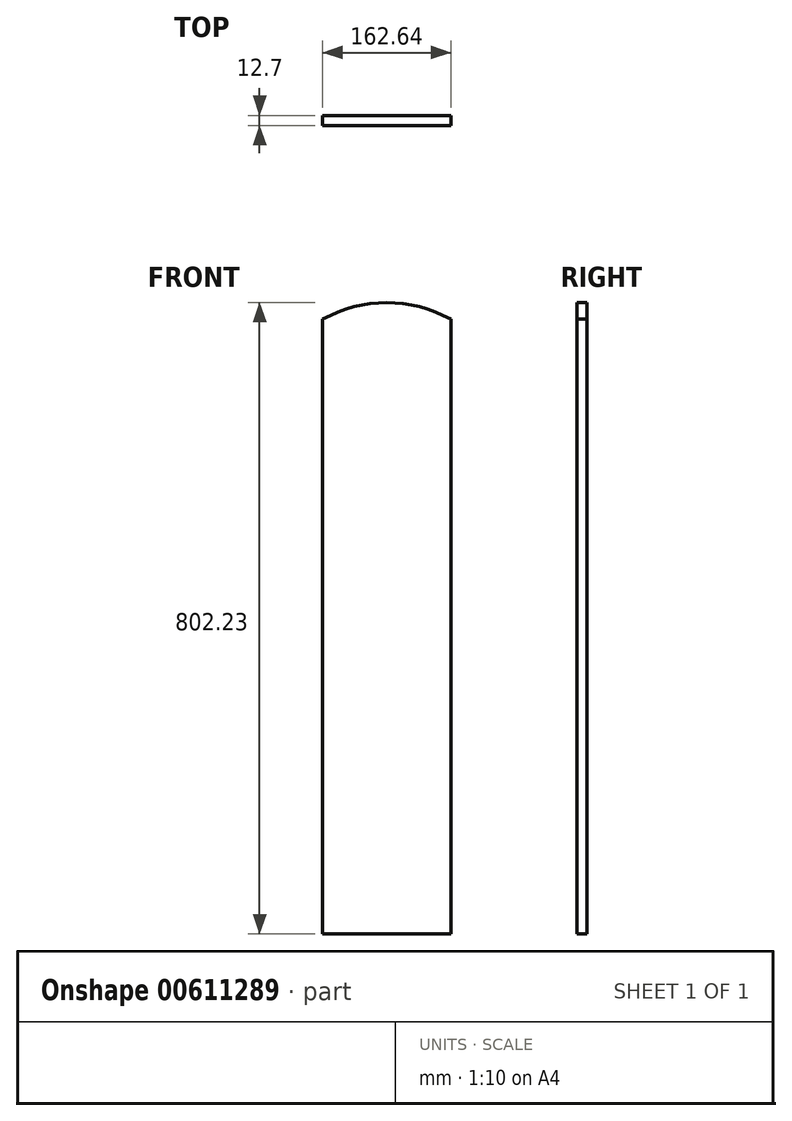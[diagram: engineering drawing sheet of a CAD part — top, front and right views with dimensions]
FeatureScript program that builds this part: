
annotation { "Feature Type Name" : "Feature", "Feature Type Description" : "" }
export const myFeature = defineFeature(function(context is Context, id is Id, definition is map)
    precondition{}
    {
        {
            var Q0;
            Q0=qCreatedBy(makeId("Front.planeOp"),FACE);
            var sketch = newSketch(context, id + "F0", { "sketchPlane" : qUnion([Q0])});
            skLineSegment(sketch, "E0", {"start": v(-81.32, 442.76) * mm, "end": v(-81.32, -338.3) * mm});
            skLineSegment(sketch, "E1", {"start": v(-81.32, -338.3) * mm, "end": v(81.32, -338.3) * mm});
            skLineSegment(sketch, "E2", {"start": v(81.32, -338.3) * mm, "end": v(81.32, 442.76) * mm});
            skArc(sketch, "E3", {"start": v(81.32, 442.76) * mm, "mid": v(0, 463.94) * mm, "end": v(-81.32, 442.76) * mm});
            skSolve(sketch);
        }
        {
            var Q0;
            Q0 = qSketchRegion(id + "F0", true);
            extrude(context, id + "F1", {"entities" : qUnion([Q0]), "depth" : 12.7 * mm, "offsetDistance" : 25.4 * mm});
        }
    });
